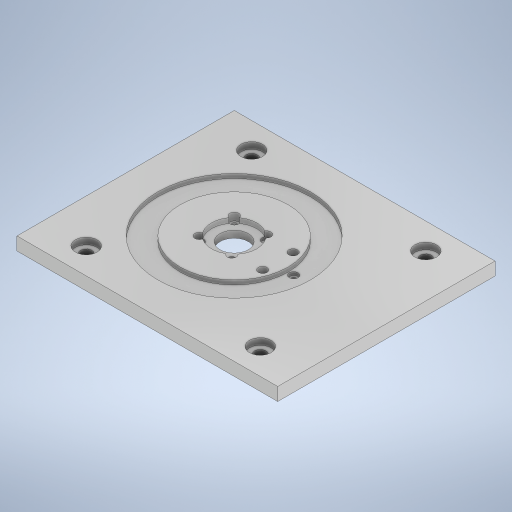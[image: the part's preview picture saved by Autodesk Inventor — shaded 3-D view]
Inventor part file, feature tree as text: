
AUTODESK INVENTOR PART (.ipt)
format: ipt  version: 2024.2 (Build 282272000, 272)  size: 357,376 bytes
history: native  units: in
note: dims shown in document units (in); Inventor stores cm internally (conversion verified against a paired STEP export)
features: reference x14, sketch x8, extrude x6, other x5, hole x2
ambient origin geometry x8: Origin, YZ Plane, XZ Plane, XY Plane, X Axis, Y Axis, Z Axis, Center Point
bodies: Solid1 (feature_tree)
feature tree (35):
  extrude  "Extrusion1"  Depth=3.937in
  extrude  "Extrusion3"  Depth=0.2362in
  hole  "Hole1"  [1 undecoded]
  extrude  "Extrusion6"  Depth=0.1378in
  extrude  "Extrusion9"  Depth=0.0787in TaperAngle=0.0deg
  hole  "Hole2"  [1 undecoded]
  extrude  "Extrusion10"  Depth=0.7929in
  extrude  "Extrusion11"  Depth=0.3937in
  sketch  "Sketch1"  dims[d0=4.7244in d1=3.937in]
  sketch  "Sketch5"  dims[d2=0.2362in d3=0.0in d16=0.8189in]
  reference  "Reference22"
  sketch  "Sketch6"  dims[d17=0.0906in d18=0.0in]
  reference  "Reference23"
  reference  "Reference24"
  reference  "Reference25"
  reference  "Reference26"
  reference  "Reference27"
  reference  "Reference28"
  reference  "Reference29"
  sketch  "Sketch8"  dims[d21=0.0827in d22=0.1575in d23=0.1732in d24=0.0787in d25=90.0deg d26=0.315in d27=0.0in d31=0.1614in]
  sketch  "Sketch11"  dims[d32=0.1378in d33=0.0in d38=0.0059in]
  reference  "Reference30"
  reference  "Reference31"
  sketch  "Sketch12"  dims[d39=0.0059in d40=0.0787in d41=0.0in]
  reference  "Reference32"
  reference  "Reference33"
  reference  "Reference34"
  reference  "Reference35"
  sketch  "Sketch13"  dims[d42=0.4724in]
  sketch  "Sketch14"  dims[d43=0.2047in d44=0.2362in d45=0.3937in d46=0.1181in d47=0.5635in d48=0.315in d49=0.8108in d50=1.5787in d51=0.7929in d52=0.3937in d53=0.0394in d54=0.0197in d55=0.0in d56=0.5118in d57=0.0in d58=0.0in d19=0.0344in d20=0.0344in]
  other  "2_Arm.iam"
  other  "HTD-45H:1"
  other  "AXK5070+AS Bearing:1"
  other  "Aluminum_Profile_4040_100.14mm_top:1"
  other  "Aluminum_Profile_4040_100.14mm_bottom:1"
note: 2 required parameter values undecoded (feature->parameter linkage not recoverable at this tier; creation-order binding heuristic only, values carry confidence <= 0.55)
